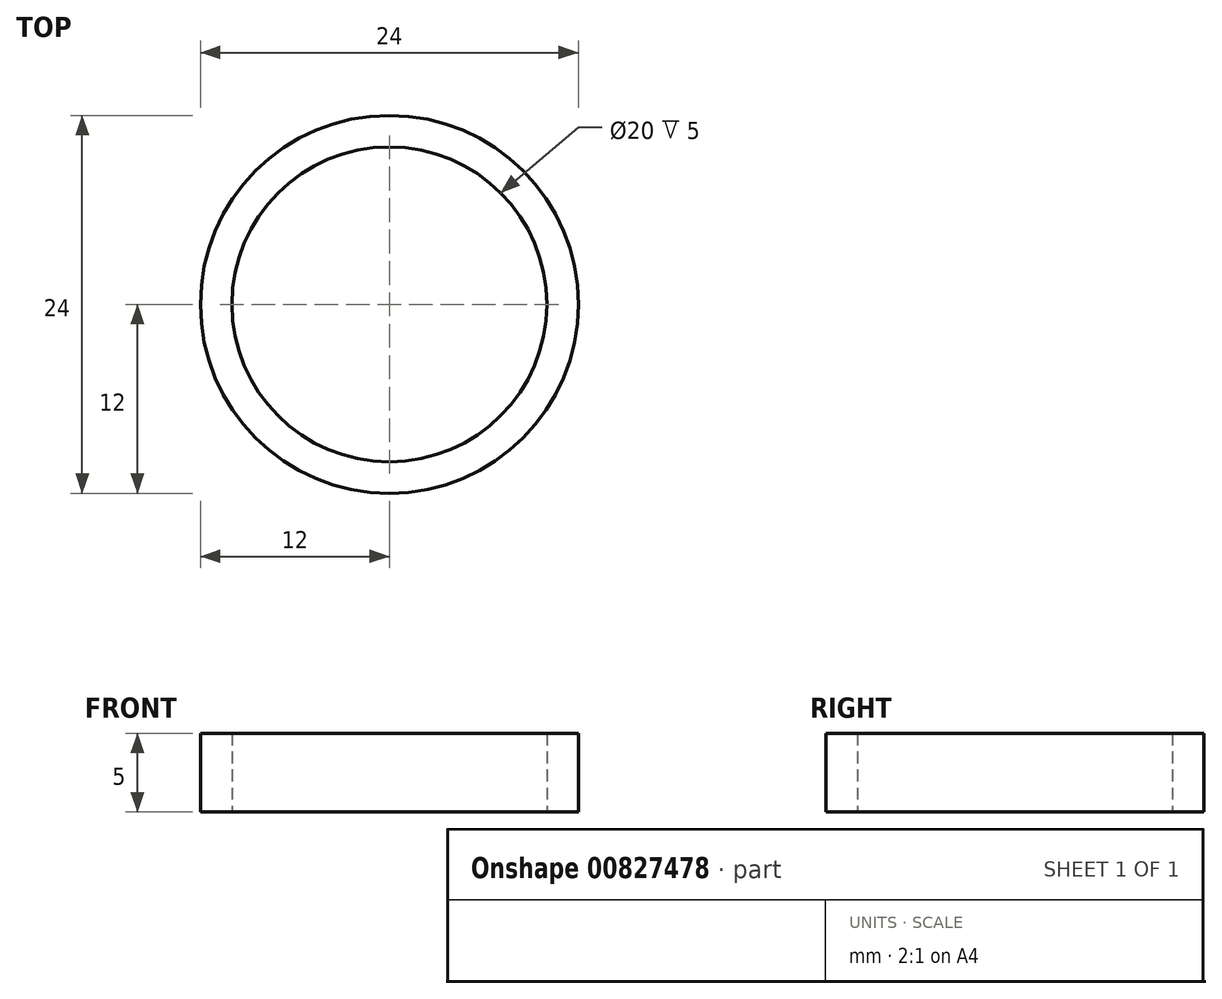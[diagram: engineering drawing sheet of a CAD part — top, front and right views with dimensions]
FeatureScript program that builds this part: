
annotation { "Feature Type Name" : "Feature", "Feature Type Description" : "" }
export const myFeature = defineFeature(function(context is Context, id is Id, definition is map)
    precondition{}
    {
        {
            var Q0;
            Q0=qCreatedBy(makeId("Top.planeOp"),FACE);
            var sketch = newSketch(context, id + "F0", { "sketchPlane" : qUnion([Q0])});
            skCircle(sketch, "E0", {"center": v(0, 0) * mm, "radius": 10 * mm});
            skCircle(sketch, "E1", {"center": v(0, 0) * mm, "radius": 12 * mm});
            skSolve(sketch);
        }
        {
            var Q0;
            Q0 = qSketchRegion(id + "F0", true);
            extrude(context, id + "F1", {"entities" : qUnion([Q0]), "depth" : 5 * mm, "offsetDistance" : 25 * mm});
        }
    });
